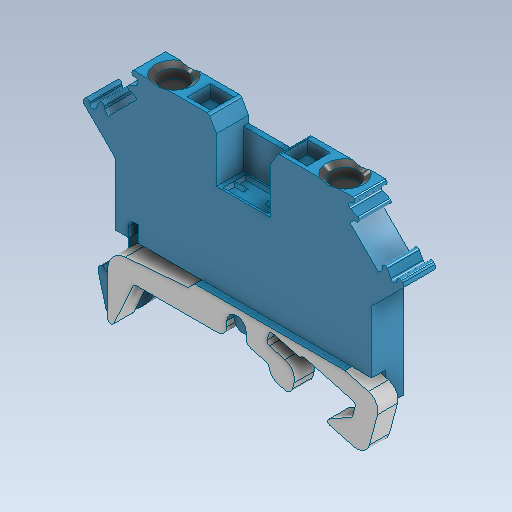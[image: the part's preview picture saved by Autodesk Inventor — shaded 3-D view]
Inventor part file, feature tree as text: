
AUTODESK INVENTOR PART (.ipt)
format: ipt  version: 2025.2 (Build 292293000, 293)  size: 828,416 bytes
history: native  units: mm
features: other x130, sketch x12, extrude x10, hole x2
ambient origin geometry x8: Origin, YZ Plane, XZ Plane, XY Plane, X Axis, Y Axis, Z Axis, Center Point
bodies: Solid1 (feature_tree)
feature tree (154):
  extrude  "Extrusion1"  Depth=2.1mm TaperAngle=0.0deg
  extrude  "Extrusion2"  Depth=2.0mm TaperAngle=0.0deg
  extrude  "Extrusion3"  Depth=7.0mm TaperAngle=0.0deg
  extrude  "Extrusion4"  Depth=5.0mm TaperAngle=0.0deg
  extrude  "Extrusion5"  Depth=3.6mm TaperAngle=0.0deg
  extrude  "Extrusion6"  TaperAngle=0.0deg  [1 undecoded]
  extrude  "Extrusion7"  TaperAngle=0.0deg  [1 undecoded]
  extrude  "Extrusion8"  TaperAngle=0.0deg  [1 undecoded]
  hole  "Hole1"  [1 undecoded]
  hole  "Hole2"  [1 undecoded]
  extrude  "Extrusion9"  Depth=10.0mm
  extrude  "Extrusion10"  Depth=10.0mm
  other  "1_2_XY"
  other  "1_2_YZ"
  other  "1_2_ZX"
  other  "1_2_X"
  other  "1_2_Y"
  other  "1_2_Z"
  other  "1_2_Center"
  other  "1_3_XY"
  other  "1_3_YZ"
  other  "1_3_ZX"
  other  "1_3_X"
  other  "1_3_Y"
  other  "1_3_Z"
  other  "1_3_Center"
  other  "1_4_XY"
  other  "1_4_YZ"
  other  "1_4_ZX"
  other  "1_4_X"
  other  "1_4_Y"
  other  "1_4_Z"
  other  "1_4_Center"
  other  "1_5_XY"
  other  "1_5_YZ"
  other  "1_5_ZX"
  other  "1_5_X"
  other  "1_5_Y"
  other  "1_5_Z"
  other  "1_5_Center"
  other  "1_6_XY"
  other  "1_6_YZ"
  other  "1_6_ZX"
  other  "1_6_X"
  other  "1_6_Y"
  other  "1_6_Z"
  other  "1_6_Center"
  other  "1_7_XY"
  other  "1_7_YZ"
  other  "1_7_ZX"
  other  "1_7_X"
  other  "1_7_Y"
  other  "1_7_Z"
  other  "1_7_Center"
  other  "1_8_XY"
  other  "1_8_YZ"
  other  "1_8_ZX"
  other  "1_8_X"
  other  "1_8_Y"
  other  "1_8_Z"
  other  "1_8_Center"
  other  "MD_XY"
  other  "MD_YZ"
  other  "MD_ZX"
  other  "MD_X"
  other  "MD_Y"
  other  "MD_Z"
  other  "MD_Center"
  other  "OP_XY"
  other  "OP_YZ"
  other  "OP_ZX"
  other  "OP_X"
  other  "OP_Y"
  other  "OP_Z"
  other  "OP_Center"
  other  "a1_XY"
  other  "a1_YZ"
  other  "a1_ZX"
  other  "a1_X"
  other  "a1_Y"
  other  "a1_Z"
  other  "a1_Center"
  other  "b2_XY"
  other  "b2_YZ"
  other  "b2_ZX"
  other  "b2_X"
  other  "b2_Y"
  other  "b2_Z"
  other  "b2_Center"
  other  "j3_XY"
  other  "j3_YZ"
  other  "j3_ZX"
  other  "j3_X"
  other  "j3_Y"
  other  "j3_Z"
  other  "j3_Center"
  other  "m4_XY"
  other  "m4_YZ"
  other  "m4_ZX"
  other  "m4_X"
  other  "m4_Y"
  other  "m4_Z"
  other  "m4_Center"
  other  "m5_XY"
  other  "m5_YZ"
  other  "m5_ZX"
  other  "m5_X"
  other  "m5_Y"
  other  "m5_Z"
  other  "m5_Center"
  other  "z6_XY"
  other  "z6_YZ"
  other  "z6_ZX"
  other  "z6_X"
  other  "z6_Y"
  other  "z6_Z"
  other  "z6_Center"
  other  "z7_XY"
  other  "z7_YZ"
  other  "z7_ZX"
  other  "z7_X"
  other  "z7_Y"
  other  "z7_Z"
  other  "z7_Center"
  other  "Edição direta1"
  other  "Edição direta2"
  other  "Edição direta3"
  other  "Edição direta4"
  other  "Edição direta5"
  other  "Edição direta6"
  other  "Edição direta7"
  other  "Edição direta8"
  other  "Edição direta9"
  sketch  "Skizze_1"  dims[d0=5.0mm d1=0.0mm d2=2.1mm d3=0.0mm]
  sketch  "Skizze_14"  dims[d39=0.0mm d40=0.0mm]
  sketch  "Skizze_15"  dims[d41=3.0mm d42=10.0mm d43=10.0mm d44=12.3mm d45=10.0mm d46=10.0mm]
  sketch  "Skizze_16"  dims[d47=12.0mm d48=10.0mm d49=10.0mm d50=0.25mm d51=0.55mm d52=-0.36mm d53=-0.4mm d54=0.0mm d55=0.0mm d56=0.0mm d57=0.0mm d58=0.35mm d59=0.5mm]
  sketch  "Skizze_2"  dims[d4=2.1mm d5=0.0mm d6=2.0mm d7=0.0mm]
  sketch  "Skizze_3"  dims[d8=0.8mm d9=0.0mm d10=7.0mm d11=0.0mm]
  sketch  "Skizze_4"  dims[d12=3.4mm d13=0.0mm d14=5.0mm d15=0.0mm]
  sketch  "Skizze_5"  dims[d16=4.2mm d17=6.0mm d18=5.8mm d19=2.0mm d20=18.545904mm d21=2.0mm d22=0.0mm]
  sketch  "Sketch9"  dims[d32=3.6mm d33=0.0mm d34=0.0mm]
  sketch  "Sketch10"  dims[d37=0.0mm d38=0.0mm]
  sketch  "Skizze_8"  dims[d23=4.2mm d24=6.0mm d25=5.8mm d26=2.0mm d27=18.545904mm d28=2.0mm d29=0.0mm d30=3.6mm d31=0.0mm]
  sketch  "Skizze_9"  dims[d35=0.0mm d36=0.0mm]
  other  "Escala1"
  other  "Escala2"
  other  "Escala3"
  other  "Tamanho1"
  other  "Tamanho2"
  other  "Tamanho3"
  other  "Mover1"
  other  "Mover2"
  other  "Tamanho4"
note: 5 required parameter values undecoded (feature->parameter linkage not recoverable at this tier; creation-order binding heuristic only, values carry confidence <= 0.55)
